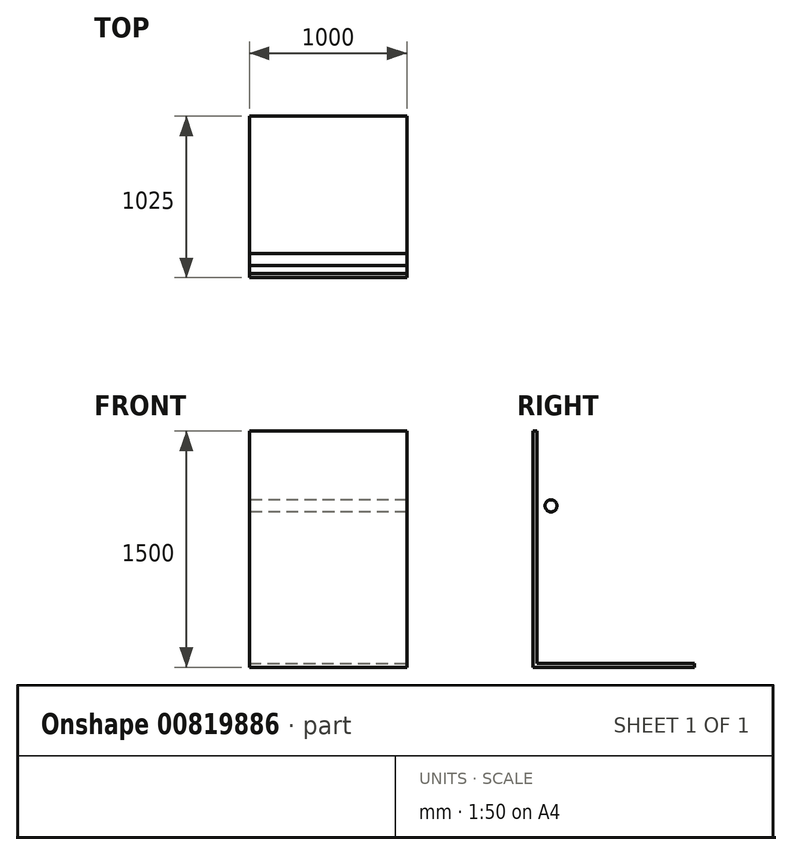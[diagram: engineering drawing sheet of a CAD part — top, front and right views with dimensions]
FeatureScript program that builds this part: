
annotation { "Feature Type Name" : "Feature", "Feature Type Description" : "" }
export const myFeature = defineFeature(function(context is Context, id is Id, definition is map)
    precondition{}
    {
        {
            var Q0;
            Q0=qCreatedBy(makeId("Front.planeOp"),FACE);
            var sketch = newSketch(context, id + "F0", { "sketchPlane" : qUnion([Q0])});
            skLineSegment(sketch, "E0.bottom", {"start": v(0, 0) * mm, "end": v(1000, 0) * mm});
            skLineSegment(sketch, "E0.top", {"start": v(0, 1500) * mm, "end": v(1000, 1500) * mm});
            skLineSegment(sketch, "E0.left", {"start": v(0, 0) * mm, "end": v(0, 1500) * mm});
            skLineSegment(sketch, "E0.right", {"start": v(1000, 0) * mm, "end": v(1000, 1500) * mm});
            skSolve(sketch);
        }
        {
            var Q0;
            Q0 = qSketchRegion(id + "F0", true);
            extrude(context, id + "F1", {"entities" : qUnion([Q0]), "depth" : 25 * mm, "offsetDistance" : 25 * mm});
        }
        {
            var Q0;
            Q0=qCreatedBy(makeId("Top.planeOp"),FACE);
            var sketch = newSketch(context, id + "F2", { "sketchPlane" : qUnion([Q0])});
            skLineSegment(sketch, "E1.bottom", {"start": v(0, 0) * mm, "end": v(1000, 0) * mm});
            skLineSegment(sketch, "E1.top", {"start": v(0, 1000) * mm, "end": v(1000, 1000) * mm});
            skLineSegment(sketch, "E1.left", {"start": v(0, 0) * mm, "end": v(0, 1000) * mm});
            skLineSegment(sketch, "E1.right", {"start": v(1000, 0) * mm, "end": v(1000, 1000) * mm});
            skSolve(sketch);
        }
        {
            var Q0;
            Q0 = qSketchRegion(id + "F2", true);
            extrude(context, id + "F3", {"entities" : qUnion([Q0]), "operationType" : NewBodyOperationType.ADD, "depth" : 25 * mm, "offsetDistance" : 25 * mm});
        }
        {
            var Q0;
            Q0=qCreatedBy(makeId("Right.planeOp"),FACE);
            var sketch = newSketch(context, id + "F4", { "sketchPlane" : qUnion([Q0])});
            skCircle(sketch, "E2", {"center": v(90.54, 1025) * mm, "radius": 38 * mm});
            skSolve(sketch);
        }
        {
            var Q0;
            Q0 = qSketchRegion(id + "F4", true);
            extrude(context, id + "F5", {"entities" : qUnion([Q0]), "depth" : 1000 * mm, "offsetDistance" : 25 * mm});
        }
    });
